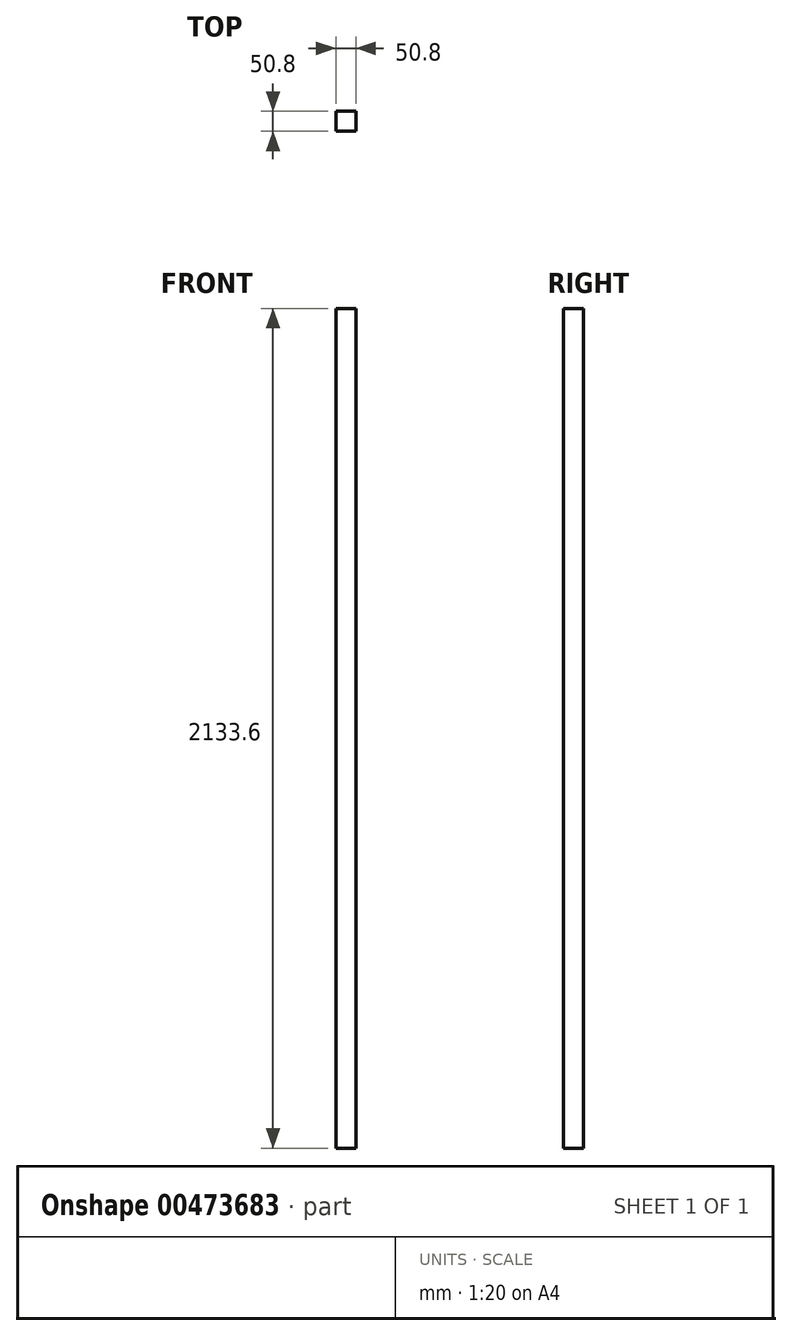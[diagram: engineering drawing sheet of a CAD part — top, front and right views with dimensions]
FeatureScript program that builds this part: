
annotation { "Feature Type Name" : "Feature", "Feature Type Description" : "" }
export const myFeature = defineFeature(function(context is Context, id is Id, definition is map)
    precondition{}
    {
        {
            var Q0;
            Q0=qCreatedBy(makeId("Top.planeOp"),FACE);
            var sketch = newSketch(context, id + "F0", { "sketchPlane" : qUnion([Q0])});
            skLineSegment(sketch, "E0.bottom", {"start": v(25.4, -25.4) * mm, "end": v(-25.4, -25.4) * mm});
            skLineSegment(sketch, "E0.top", {"start": v(25.4, 25.4) * mm, "end": v(-25.4, 25.4) * mm});
            skLineSegment(sketch, "E0.left", {"start": v(25.4, -25.4) * mm, "end": v(25.4, 25.4) * mm});
            skLineSegment(sketch, "E0.right", {"start": v(-25.4, -25.4) * mm, "end": v(-25.4, 25.4) * mm});
            skPoint(sketch, "E0.middle", {"position": v(0, 0) * mm});
            skSolve(sketch);
        }
        {
            var Q0;
            Q0=qSketchRegion(id+"F0",true);
            extrude(context, id + "F1", {"entities" : qUnion([Q0]), "depth" : 2133.6 * mm});
        }
    });
